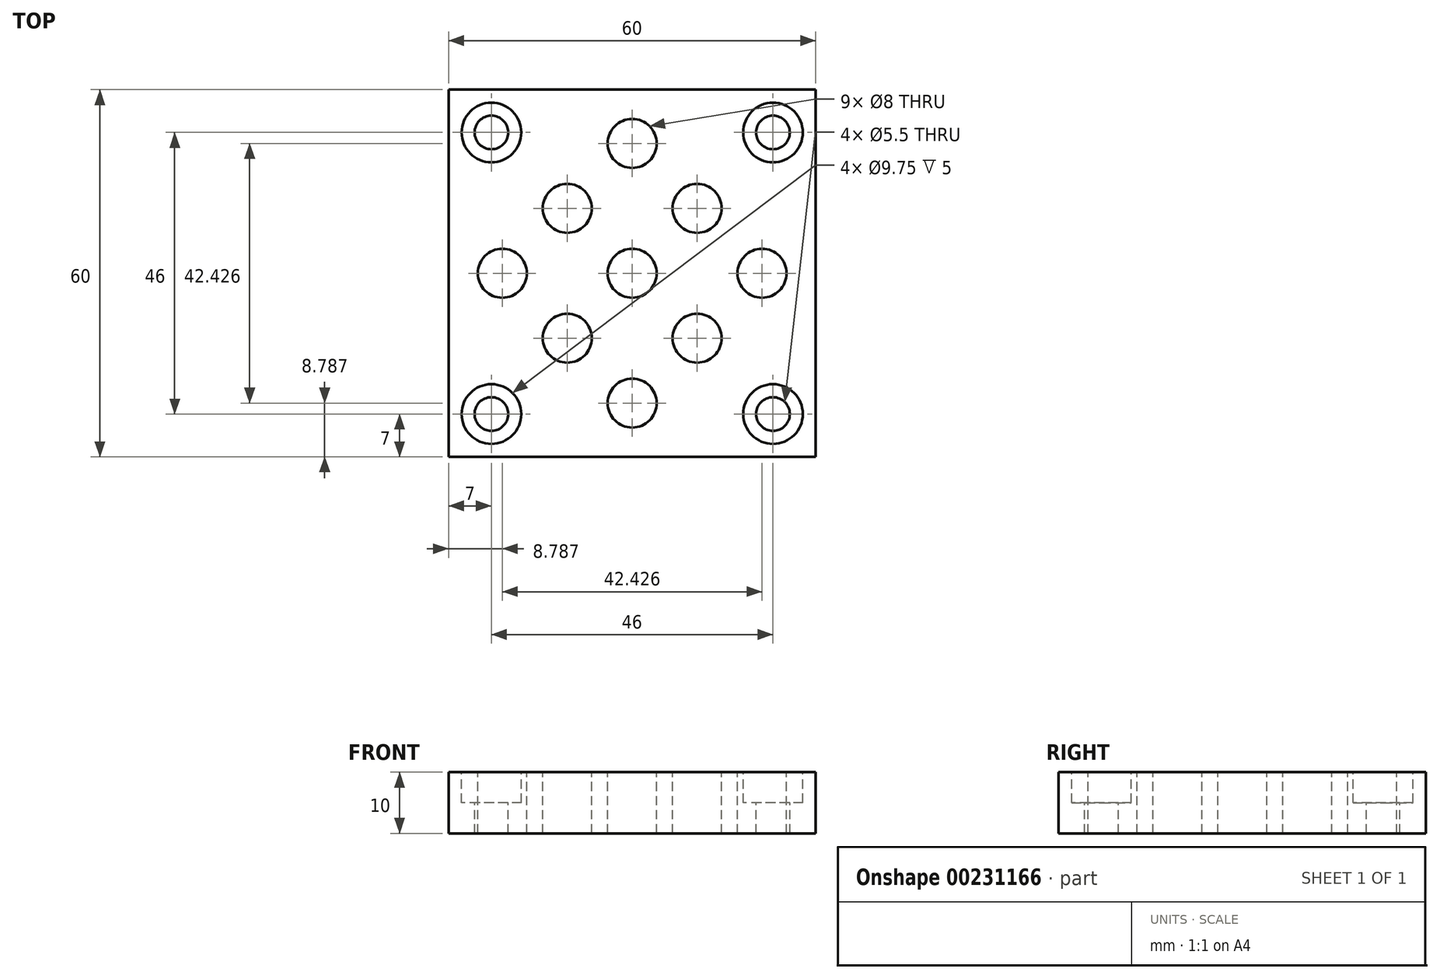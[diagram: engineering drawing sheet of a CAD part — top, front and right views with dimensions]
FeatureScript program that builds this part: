
annotation { "Feature Type Name" : "Feature", "Feature Type Description" : "" }
export const myFeature = defineFeature(function(context is Context, id is Id, definition is map)
    precondition{}
    {
        {
            var Q0;
            Q0=qCreatedBy(makeId("Top.planeOp"),FACE);
            var sketch = newSketch(context, id + "F0", { "sketchPlane" : qUnion([Q0])});
            skLineSegment(sketch, "E0.bottom", {"start": v(30, 30) * mm, "end": v(-30, 30) * mm});
            skLineSegment(sketch, "E0.top", {"start": v(30, -30) * mm, "end": v(-30, -30) * mm});
            skLineSegment(sketch, "E0.left", {"start": v(30, 30) * mm, "end": v(30, -30) * mm});
            skLineSegment(sketch, "E0.right", {"start": v(-30, 30) * mm, "end": v(-30, -30) * mm});
            skPoint(sketch, "E0.middle", {"position": v(0, 0) * mm});
            skSolve(sketch);
        }
        {
            var Q0;
            Q0 = qSketchRegion(id + "F0", true);
            extrude(context, id + "F1", {"entities" : qUnion([Q0]), "oppositeDirection" : true, "depth" : 10 * mm});
        }
        {
            var Q0;
            Q0=makeQuery(id+"F1.opExtrude","CAP_FACE",FACE,{"disambiguationData":[OSD([sQuery(id+"F0.wireOp",EDGE,"E0.bottom"),sQuery(id+"F0.wireOp",EDGE,"E0.top"),sQuery(id+"F0.wireOp",EDGE,"E0.left"),sQuery(id+"F0.wireOp",EDGE,"E0.right")])],"isStart":true});
            var sketch = newSketch(context, id + "F2", { "sketchPlane" : qUnion([Q0])});
            skLineSegment(sketch, "E1.bottom", {"start": v(-23, 23) * mm, "end": v(23, 23) * mm, "construction": true});
            skLineSegment(sketch, "E1.top", {"start": v(-23, -23) * mm, "end": v(23, -23) * mm, "construction": true});
            skLineSegment(sketch, "E1.left", {"start": v(-23, 23) * mm, "end": v(-23, -23) * mm, "construction": true});
            skLineSegment(sketch, "E1.right", {"start": v(23, 23) * mm, "end": v(23, -23) * mm, "construction": true});
            skPoint(sketch, "E1.middle", {"position": v(0, 0) * mm});
            skLineSegment(sketch, "E2", {"start": v(23, 23) * mm, "end": v(-23, -23) * mm, "construction": true});
            skLineSegment(sketch, "E3", {"start": v(23, -23) * mm, "end": v(-23, 23) * mm, "construction": true});
            skCircle(sketch, "E4", {"center": v(0, 21.21) * mm, "radius": 4 * mm});
            skCircle(sketch, "E5.1.0.0", {"center": v(10.6, 10.6) * mm, "radius": 4 * mm});
            skCircle(sketch, "E5.2.0.0", {"center": v(21.21, 0) * mm, "radius": 4 * mm});
            skLineSegment(sketch, "E5.direction1", {"start": v(0, 21.21) * mm, "end": v(10.6, 10.6) * mm, "construction": true});
            skCircle(sketch, "E6.1.0.0", {"center": v(-10.6, 10.6) * mm, "radius": 4 * mm});
            skCircle(sketch, "E6.1.0.1", {"center": v(0, 0) * mm, "radius": 4 * mm});
            skCircle(sketch, "E6.1.0.2", {"center": v(10.6, -10.6) * mm, "radius": 4 * mm});
            skLineSegment(sketch, "E6.1.0.3", {"start": v(12.4, 12.4) * mm, "end": v(-33.6, -33.6) * mm, "construction": true});
            skCircle(sketch, "E6.2.0.0", {"center": v(-21.21, 0) * mm, "radius": 4 * mm});
            skCircle(sketch, "E6.2.0.1", {"center": v(-10.6, -10.6) * mm, "radius": 4 * mm});
            skCircle(sketch, "E6.2.0.2", {"center": v(0, -21.21) * mm, "radius": 4 * mm});
            skLineSegment(sketch, "E6.2.0.3", {"start": v(1.79, 1.79) * mm, "end": v(-44.21, -44.21) * mm, "construction": true});
            skLineSegment(sketch, "E6.direction1", {"start": v(0, 21.21) * mm, "end": v(-10.6, 10.6) * mm, "construction": true});
            skSolve(sketch);
        }
        {
            var Q0;
            Q0=makeQuery(id+"F2.imprint","IMPRINT",FACE,{"disambiguationData":[TD([[makeQuery(id+"F2.imprint","IMPRINT",EDGE,{"derivedFrom":sQuery(id+"F2.wireOp",EDGE,"E6.2.0.2")}),1.0]])]});
            var Q1;
            Q1=makeQuery(id+"F2.imprint","IMPRINT",FACE,{"disambiguationData":[TD([[makeQuery(id+"F2.imprint","IMPRINT",EDGE,{"derivedFrom":sQuery(id+"F2.wireOp",EDGE,"E6.2.0.1")}),1.0]])]});
            var Q2;
            Q2=makeQuery(id+"F2.imprint","IMPRINT",FACE,{"disambiguationData":[TD([[makeQuery(id+"F2.imprint","IMPRINT",EDGE,{"derivedFrom":sQuery(id+"F2.wireOp",EDGE,"E6.2.0.0")}),1.0]])]});
            var Q3;
            Q3=makeQuery(id+"F2.imprint","IMPRINT",FACE,{"disambiguationData":[TD([[makeQuery(id+"F2.imprint","IMPRINT",EDGE,{"derivedFrom":sQuery(id+"F2.wireOp",EDGE,"E6.1.0.1")}),1.0]])]});
            var Q4;
            Q4=makeQuery(id+"F2.imprint","IMPRINT",FACE,{"disambiguationData":[TD([[makeQuery(id+"F2.imprint","IMPRINT",EDGE,{"derivedFrom":sQuery(id+"F2.wireOp",EDGE,"E6.1.0.2")}),1.0]])]});
            var Q5;
            Q5=makeQuery(id+"F2.imprint","IMPRINT",FACE,{"disambiguationData":[TD([[makeQuery(id+"F2.imprint","IMPRINT",EDGE,{"derivedFrom":sQuery(id+"F2.wireOp",EDGE,"E5.2.0.0")}),1.0]])]});
            var Q6;
            Q6=makeQuery(id+"F2.imprint","IMPRINT",FACE,{"disambiguationData":[TD([[makeQuery(id+"F2.imprint","IMPRINT",EDGE,{"derivedFrom":sQuery(id+"F2.wireOp",EDGE,"E5.1.0.0")}),1.0]])]});
            var Q7;
            Q7=makeQuery(id+"F2.imprint","IMPRINT",FACE,{"disambiguationData":[TD([[makeQuery(id+"F2.imprint","IMPRINT",EDGE,{"derivedFrom":sQuery(id+"F2.wireOp",EDGE,"E4")}),1.0]])]});
            var Q8;
            Q8=makeQuery(id+"F2.imprint","IMPRINT",FACE,{"disambiguationData":[TD([[makeQuery(id+"F2.imprint","IMPRINT",EDGE,{"derivedFrom":sQuery(id+"F2.wireOp",EDGE,"E6.1.0.0")}),1.0]])]});
            extrude(context, id + "F3", {"entities" : qUnion([Q0, Q1, Q2, Q3, Q4, Q5, Q6, Q7, Q8]), "operationType" : NewBodyOperationType.REMOVE, "endBound" : BoundingType.THROUGH_ALL, "oppositeDirection" : true, "depth" : 25 * mm});
        }
        {
            var Q0;
            Q0=sQuery(id+"F2.wireOp",VERTEX,"E1.top.end");
            var Q1;
            Q1=sQuery(id+"F2.wireOp",VERTEX,"E1.left.end");
            var Q2;
            Q2=sQuery(id+"F2.wireOp",VERTEX,"E1.bottom.start");
            var Q3;
            Q3=sQuery(id+"F2.wireOp",VERTEX,"E1.right.start");
            var Q4;
            Q4=makeQuery(id+"F1.opExtrude","SWEPT_BODY",BODY,{"disambiguationData":[OSD([sQuery(id+"F0.wireOp",EDGE,"E0.bottom"),sQuery(id+"F0.wireOp",EDGE,"E0.top"),sQuery(id+"F0.wireOp",EDGE,"E0.left"),sQuery(id+"F0.wireOp",EDGE,"E0.right")])]});
            hole(context, id + "F4", {"style" : HoleStyle.C_BORE, "endStyle" : HoleEndStyle.THROUGH, "standardTappedOrClearance" : lookupTablePath({ "standard" : "ISO", "fit" : "Normal", "size" : "M5", "type" : "Clearance" }), "standardBlindInLast" : lookupTablePath({ "fit" : "Standard", "standard" : "ISO", "size" : "M5", "type" : "Clearance" }), "holeDiameter" : 5.5 * mm, "cBoreDiameter" : 9.75 * mm, "cBoreDepth" : 5 * mm, "locations" : qUnion([Q0, Q1, Q2, Q3]), "scope" : qUnion([Q4]), "isTappedThrough" : true});
        }
    });
